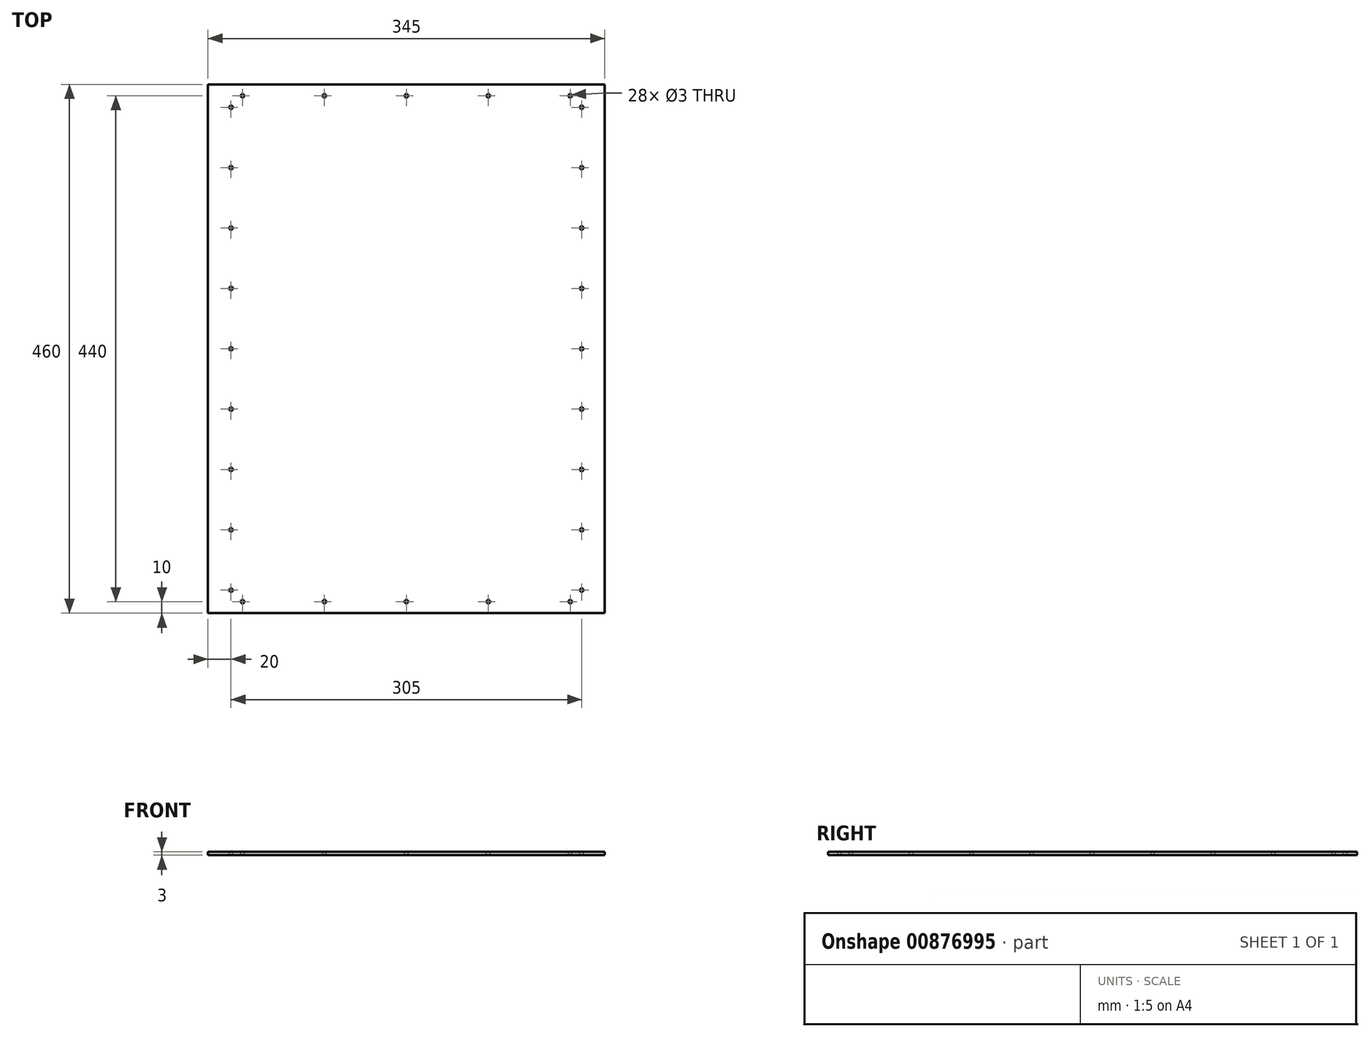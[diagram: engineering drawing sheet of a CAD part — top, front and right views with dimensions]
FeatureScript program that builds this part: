
annotation { "Feature Type Name" : "Feature", "Feature Type Description" : "" }
export const myFeature = defineFeature(function(context is Context, id is Id, definition is map)
    precondition{}
    {
        {
            var Q0;
            Q0=qCreatedBy(makeId("Top.planeOp"),FACE);
            var sketch = newSketch(context, id + "F0", { "sketchPlane" : qUnion([Q0])});
            skLineSegment(sketch, "E0.bottom", {"start": v(-172.5, 230) * mm, "end": v(172.5, 230) * mm});
            skLineSegment(sketch, "E0.top", {"start": v(-172.5, -230) * mm, "end": v(172.5, -230) * mm});
            skLineSegment(sketch, "E0.left", {"start": v(-172.5, 230) * mm, "end": v(-172.5, -230) * mm});
            skLineSegment(sketch, "E0.right", {"start": v(172.5, 230) * mm, "end": v(172.5, -230) * mm});
            skSolve(sketch);
        }
        {
            var Q0;
            Q0=makeQuery(id+"F0.imprint","IMPRINT",FACE,{"disambiguationData":[TD([[makeQuery(id+"F0.imprint","IMPRINT",EDGE,{"derivedFrom":sQuery(id+"F0.wireOp",EDGE,"E0.bottom")}),-1.0]])]});
            extrude(context, id + "F1", {"entities" : qUnion([Q0]), "depth" : 3 * mm, "offsetDistance" : 25 * mm});
        }
        {
            var Q0;
            Q0=makeQuery(id+"F1.opExtrude","CAP_FACE",FACE,{"disambiguationData":[OSD([sQuery(id+"F0.wireOp",EDGE,"E0.bottom"),sQuery(id+"F0.wireOp",EDGE,"E0.top"),sQuery(id+"F0.wireOp",EDGE,"E0.left"),sQuery(id+"F0.wireOp",EDGE,"E0.right")])],"isStart":false});
            var sketch = newSketch(context, id + "F2", { "sketchPlane" : qUnion([Q0])});
            skLineSegment(sketch, "E1", {"start": v(0, 230) * mm, "end": v(0, -230) * mm, "construction": true});
            skLineSegment(sketch, "E2", {"start": v(-172.5, 0) * mm, "end": v(172.5, 0) * mm, "construction": true});
            skLineSegment(sketch, "E3", {"start": v(-152.5, -230) * mm, "end": v(-152.5, 230) * mm, "construction": true});
            skLineSegment(sketch, "E4", {"start": v(152.5, -230) * mm, "end": v(152.5, 230) * mm, "construction": true});
            skLineSegment(sketch, "E5", {"start": v(-172.5, 210) * mm, "end": v(172.5, 210) * mm, "construction": true});
            skLineSegment(sketch, "E6", {"start": v(-172.5, 157.5) * mm, "end": v(172.5, 157.5) * mm, "construction": true});
            skLineSegment(sketch, "E7", {"start": v(-172.5, 105) * mm, "end": v(172.5, 105) * mm, "construction": true});
            skLineSegment(sketch, "E8", {"start": v(-172.5, 52.5) * mm, "end": v(172.5, 52.5) * mm, "construction": true});
            skLineSegment(sketch, "E9.MirrorCS", {"start": v(-172.5, -210) * mm, "end": v(172.5, -210) * mm, "construction": true});
            skLineSegment(sketch, "E10.MirrorCS", {"start": v(-172.5, -157.5) * mm, "end": v(172.5, -157.5) * mm, "construction": true});
            skLineSegment(sketch, "E11.MirrorCS", {"start": v(-172.5, -105) * mm, "end": v(172.5, -105) * mm, "construction": true});
            skLineSegment(sketch, "E12.MirrorCS", {"start": v(-172.5, -52.5) * mm, "end": v(172.5, -52.5) * mm, "construction": true});
            skSolve(sketch);
        }
        {
            var Q0;
            Q0=makeQuery(id+"F2.imprint","IMPRINT",FACE,{"disambiguationData":[TD([[makeQuery(id+"F2.imprint","IMPRINT",EDGE,{"derivedFrom":makeQuery(id+"F1.opExtrude","CAP_EDGE",EDGE,{"disambiguationData":[OSD([sQuery(id+"F0.wireOp",EDGE,"E0.bottom")])],"isStart":false})}),-1.0]])]});
            var sketch = newSketch(context, id + "F3", { "sketchPlane" : qUnion([Q0])});
            skCircle(sketch, "E13", {"center": v(-152.5, 210) * mm, "radius": 1.5 * mm});
            skCircle(sketch, "E14", {"center": v(-152.5, 157.5) * mm, "radius": 1.5 * mm});
            skCircle(sketch, "E15", {"center": v(-152.5, 105) * mm, "radius": 1.5 * mm});
            skCircle(sketch, "E16", {"center": v(-152.5, 0) * mm, "radius": 1.5 * mm});
            skCircle(sketch, "E17.MirrorC", {"center": v(152.5, 105) * mm, "radius": 1.5 * mm});
            skCircle(sketch, "E18.MirrorC", {"center": v(152.5, 157.5) * mm, "radius": 1.5 * mm});
            skCircle(sketch, "E19.MirrorC", {"center": v(152.5, 210) * mm, "radius": 1.5 * mm});
            skCircle(sketch, "E20.MirrorC", {"center": v(152.5, 0) * mm, "radius": 1.5 * mm});
            skCircle(sketch, "E21", {"center": v(-152.5, 52.5) * mm, "radius": 1.5 * mm});
            skCircle(sketch, "E22.MirrorC", {"center": v(152.5, 52.5) * mm, "radius": 1.5 * mm});
            skCircle(sketch, "E23.MirrorC", {"center": v(-152.5, -210) * mm, "radius": 1.5 * mm});
            skCircle(sketch, "E24.MirrorC", {"center": v(-152.5, -157.5) * mm, "radius": 1.5 * mm});
            skCircle(sketch, "E25.MirrorC", {"center": v(-152.5, -105) * mm, "radius": 1.5 * mm});
            skCircle(sketch, "E26.MirrorC", {"center": v(-152.5, -52.5) * mm, "radius": 1.5 * mm});
            skCircle(sketch, "E27.MirrorC", {"center": v(152.5, -52.5) * mm, "radius": 1.5 * mm});
            skCircle(sketch, "E28.MirrorC", {"center": v(152.5, -105) * mm, "radius": 1.5 * mm});
            skCircle(sketch, "E29.MirrorC", {"center": v(152.5, -157.5) * mm, "radius": 1.5 * mm});
            skCircle(sketch, "E30.MirrorC", {"center": v(152.5, -210) * mm, "radius": 1.5 * mm});
            skSolve(sketch);
        }
        {
            var Q0;
            Q0=makeQuery(id+"F2.imprint","IMPRINT",FACE,{"disambiguationData":[TD([[makeQuery(id+"F2.imprint","IMPRINT",EDGE,{"derivedFrom":makeQuery(id+"F1.opExtrude","CAP_EDGE",EDGE,{"disambiguationData":[OSD([sQuery(id+"F0.wireOp",EDGE,"E0.bottom")])],"isStart":false})}),-1.0]])]});
            var sketch = newSketch(context, id + "F4", { "sketchPlane" : qUnion([Q0])});
            skCircle(sketch, "E31", {"center": v(-142.5, 220) * mm, "radius": 1.5 * mm});
            skCircle(sketch, "E32", {"center": v(0, 220) * mm, "radius": 1.5 * mm});
            skCircle(sketch, "E33", {"center": v(142.5, 220) * mm, "radius": 1.5 * mm});
            skCircle(sketch, "E34", {"center": v(-71.25, 220) * mm, "radius": 1.5 * mm});
            skCircle(sketch, "E35.MirrorC", {"center": v(71.25, 220) * mm, "radius": 1.5 * mm});
            skCircle(sketch, "E36.MirrorC", {"center": v(-142.5, -220) * mm, "radius": 1.5 * mm});
            skCircle(sketch, "E37.MirrorC", {"center": v(-71.25, -220) * mm, "radius": 1.5 * mm});
            skCircle(sketch, "E38.MirrorC", {"center": v(0, -220) * mm, "radius": 1.5 * mm});
            skCircle(sketch, "E39.MirrorC", {"center": v(71.25, -220) * mm, "radius": 1.5 * mm});
            skCircle(sketch, "E40.MirrorC", {"center": v(142.5, -220) * mm, "radius": 1.5 * mm});
            skSolve(sketch);
        }
        {
            var Q0;
            Q0=sQuery(id+"F3.wireOp",VERTEX,"E13.center");
            var Q1;
            Q1=sQuery(id+"F3.wireOp",VERTEX,"E14.center");
            var Q2;
            Q2=sQuery(id+"F3.wireOp",VERTEX,"E15.center");
            var Q3;
            Q3=sQuery(id+"F3.wireOp",VERTEX,"E21.center");
            var Q4;
            Q4=sQuery(id+"F3.wireOp",VERTEX,"E16.center");
            var Q5;
            Q5=sQuery(id+"F3.wireOp",VERTEX,"E26.MirrorC.center");
            var Q6;
            Q6=sQuery(id+"F3.wireOp",VERTEX,"E25.MirrorC.center");
            var Q7;
            Q7=sQuery(id+"F3.wireOp",VERTEX,"E24.MirrorC.center");
            var Q8;
            Q8=sQuery(id+"F3.wireOp",VERTEX,"E23.MirrorC.center");
            var Q9;
            Q9=sQuery(id+"F3.wireOp",VERTEX,"E30.MirrorC.center");
            var Q10;
            Q10=sQuery(id+"F3.wireOp",VERTEX,"E29.MirrorC.center");
            var Q11;
            Q11=sQuery(id+"F3.wireOp",VERTEX,"E28.MirrorC.center");
            var Q12;
            Q12=sQuery(id+"F3.wireOp",VERTEX,"E27.MirrorC.center");
            var Q13;
            Q13=sQuery(id+"F3.wireOp",VERTEX,"E20.MirrorC.center");
            var Q14;
            Q14=sQuery(id+"F3.wireOp",VERTEX,"E22.MirrorC.center");
            var Q15;
            Q15=sQuery(id+"F3.wireOp",VERTEX,"E17.MirrorC.center");
            var Q16;
            Q16=sQuery(id+"F3.wireOp",VERTEX,"E18.MirrorC.center");
            var Q17;
            Q17=sQuery(id+"F3.wireOp",VERTEX,"E19.MirrorC.center");
            var Q18;
            Q18=makeQuery(id+"F1.opExtrude","SWEPT_BODY",BODY,{"disambiguationData":[OSD([sQuery(id+"F0.wireOp",EDGE,"E0.bottom"),sQuery(id+"F0.wireOp",EDGE,"E0.top"),sQuery(id+"F0.wireOp",EDGE,"E0.left"),sQuery(id+"F0.wireOp",EDGE,"E0.right")])]});
            hole(context, id + "F5", {"style" : HoleStyle.SIMPLE, "endStyle" : HoleEndStyle.THROUGH, "holeDiameter" : 3 * mm, "majorDiameter" : 5 * mm, "isTappedThrough" : true, "tappedDepth" : 12 * mm, "tapClearance" : 3, "locations" : qUnion([Q0, Q1, Q2, Q3, Q4, Q5, Q6, Q7, Q8, Q9, Q10, Q11, Q12, Q13, Q14, Q15, Q16, Q17]), "scope" : qUnion([Q18])});
        }
        {
            var Q0;
            Q0=sQuery(id+"F4.wireOp",VERTEX,"E31.center");
            var Q1;
            Q1=sQuery(id+"F4.wireOp",VERTEX,"E34.center");
            var Q2;
            Q2=sQuery(id+"F4.wireOp",VERTEX,"E32.center");
            var Q3;
            Q3=sQuery(id+"F4.wireOp",VERTEX,"E35.MirrorC.center");
            var Q4;
            Q4=sQuery(id+"F4.wireOp",VERTEX,"E33.center");
            var Q5;
            Q5=sQuery(id+"F4.wireOp",VERTEX,"E36.MirrorC.center");
            var Q6;
            Q6=sQuery(id+"F4.wireOp",VERTEX,"E37.MirrorC.center");
            var Q7;
            Q7=sQuery(id+"F4.wireOp",VERTEX,"E38.MirrorC.center");
            var Q8;
            Q8=sQuery(id+"F4.wireOp",VERTEX,"E39.MirrorC.center");
            var Q9;
            Q9=sQuery(id+"F4.wireOp",VERTEX,"E40.MirrorC.center");
            var Q10;
            Q10=makeQuery(id+"F1.opExtrude","SWEPT_BODY",BODY,{"disambiguationData":[OSD([sQuery(id+"F0.wireOp",EDGE,"E0.bottom"),sQuery(id+"F0.wireOp",EDGE,"E0.top"),sQuery(id+"F0.wireOp",EDGE,"E0.left"),sQuery(id+"F0.wireOp",EDGE,"E0.right")])]});
            hole(context, id + "F6", {"style" : HoleStyle.SIMPLE, "endStyle" : HoleEndStyle.THROUGH, "holeDiameter" : 3 * mm, "majorDiameter" : 5 * mm, "isTappedThrough" : true, "tappedDepth" : 12 * mm, "tapClearance" : 3, "locations" : qUnion([Q0, Q1, Q2, Q3, Q4, Q5, Q6, Q7, Q8, Q9]), "scope" : qUnion([Q10])});
        }
    });
